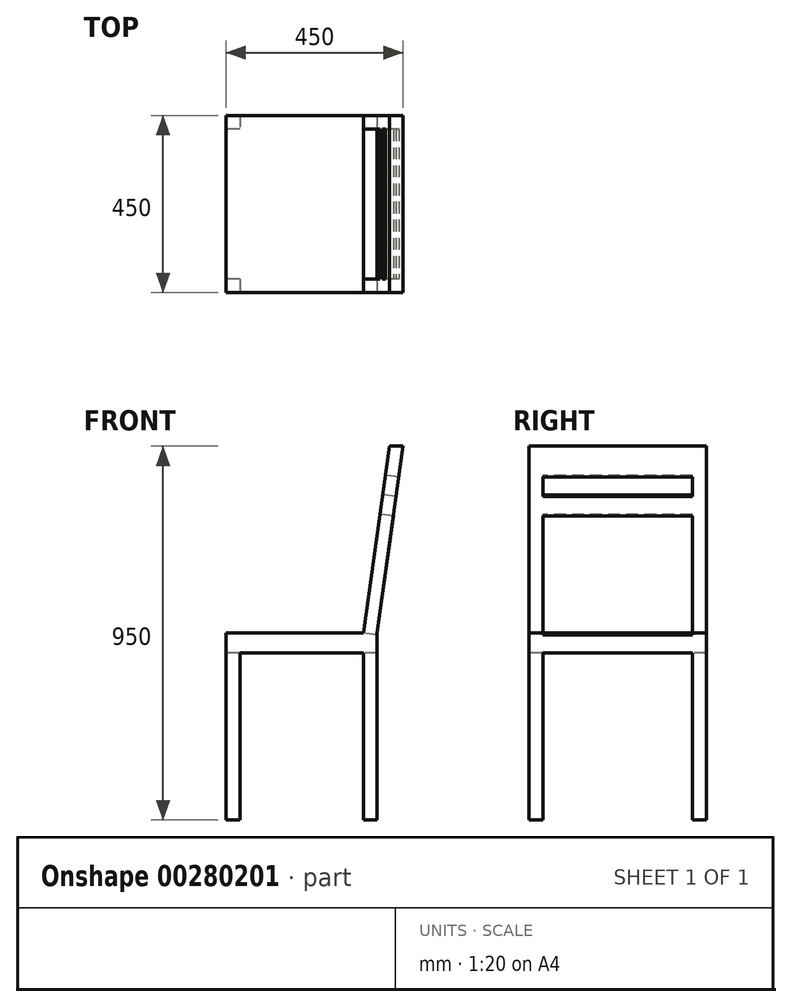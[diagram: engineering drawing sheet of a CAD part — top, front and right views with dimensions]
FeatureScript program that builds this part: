
annotation { "Feature Type Name" : "Feature", "Feature Type Description" : "" }
export const myFeature = defineFeature(function(context is Context, id is Id, definition is map)
    precondition{}
    {
        {
            var Q0;
            Q0=qCreatedBy(makeId("Top.planeOp"),FACE);
            var sketch = newSketch(context, id + "F0", { "sketchPlane" : qUnion([Q0])});
            skLineSegment(sketch, "E0.bottom", {"start": v(225, 225) * mm, "end": v(-225, 225) * mm});
            skLineSegment(sketch, "E0.top", {"start": v(225, -225) * mm, "end": v(-225, -225) * mm});
            skLineSegment(sketch, "E0.left", {"start": v(225, 225) * mm, "end": v(225, -225) * mm});
            skLineSegment(sketch, "E0.right", {"start": v(-225, 225) * mm, "end": v(-225, -225) * mm});
            skPoint(sketch, "E0.middle", {"position": v(0, 0) * mm});
            skSolve(sketch);
        }
        {
            var Q0;
            Q0=qSketchRegion(id+"F0",true);
            extrude(context, id + "F1", {"entities" : qUnion([Q0]), "depth" : 950 * mm});
        }
        {
            var Q0;
            Q0=makeQuery(id+"F1.opExtrude","SWEPT_FACE",FACE,{"disambiguationData":[OSD([sQuery(id+"F0.wireOp",EDGE,"E0.top")])]});
            var sketch = newSketch(context, id + "F2", { "sketchPlane" : qUnion([Q0])});
            skLineSegment(sketch, "E1.bottom", {"start": v(225, 475) * mm, "end": v(-225, 475) * mm});
            skLineSegment(sketch, "E1.top", {"start": v(225, 425) * mm, "end": v(-225, 425) * mm});
            skLineSegment(sketch, "E1.left", {"start": v(225, 475) * mm, "end": v(225, 425) * mm});
            skLineSegment(sketch, "E1.right", {"start": v(-225, 475) * mm, "end": v(-225, 425) * mm});
            skLineSegment(sketch, "E2", {"start": v(225, 950) * mm, "end": v(158.8, 475) * mm});
            skLineSegment(sketch, "E3", {"start": v(190, 950) * mm, "end": v(123.8, 475) * mm});
            skLineSegment(sketch, "E4", {"start": v(158.8, 475) * mm, "end": v(158.8, 0) * mm});
            skLineSegment(sketch, "E5", {"start": v(123.8, 475) * mm, "end": v(123.8, 0) * mm});
            skLineSegment(sketch, "E6.bottom", {"start": v(-225, 0) * mm, "end": v(-190, 0) * mm});
            skLineSegment(sketch, "E6.top", {"start": v(-225, 425) * mm, "end": v(-190, 425) * mm});
            skLineSegment(sketch, "E6.left", {"start": v(-225, 0) * mm, "end": v(-225, 425) * mm});
            skLineSegment(sketch, "E6.right", {"start": v(-190, 0) * mm, "end": v(-190, 425) * mm});
            skSolve(sketch);
        }
        {
            var Q0;
            {var subQ4=sQuery(id+"F2.wireOp",EDGE,"E3");Q0=makeQuery(id+"F2.imprint","IMPRINT",FACE,{"disambiguationData":[TD([[makeQuery(id+"F2.imprint","IMPRINT",EDGE,{"derivedFrom":subQ4}),-1.0]])]});}
            var Q1;
            {var subQ4=sQuery(id+"F2.wireOp",EDGE,"E2");Q1=makeQuery(id+"F2.imprint","IMPRINT",FACE,{"disambiguationData":[TD([[makeQuery(id+"F2.imprint","IMPRINT",EDGE,{"derivedFrom":subQ4}),1.0]])]});}
            var Q2;
            {var subQ1=sQuery(id+"F0.wireOp",EDGE,"E0.top");var subQ4=sQuery(id+"F2.wireOp",EDGE,"E4");var subQ6=makeQuery(id+"F1.opExtrude","CAP_EDGE",EDGE,{"disambiguationData":[OSD([subQ1])],"isStart":true});var subQ7=makeQuery(id+"F2.imprint","INTERSECT",VERTEX,{"derivedFrom":[subQ6,subQ4]});Q2=makeQuery(id+"F2.imprint","IMPRINT",FACE,{"disambiguationData":[TD([[makeQuery(id+"F2.imprint","IMPRINT",EDGE,{"disambiguationData":[TD([[subQ7,1.0]])],"derivedFrom":subQ4}),1.0]])]});}
            var Q3;
            {var subQ0=sQuery(id+"F2.wireOp",EDGE,"E6.right");Q3=makeQuery(id+"F2.imprint","IMPRINT",FACE,{"disambiguationData":[TD([[makeQuery(id+"F2.imprint","IMPRINT",EDGE,{"derivedFrom":subQ0}),-1.0]])]});}
            var Q4;
            {var subQ0=sQuery(id+"F2.wireOp",EDGE,"E1.left");Q4=makeQuery(id+"F2.imprint","IMPRINT",FACE,{"disambiguationData":[TD([[makeQuery(id+"F2.imprint","IMPRINT",EDGE,{"derivedFrom":subQ0}),-1.0]])]});}
            extrude(context, id + "F3", {"entities" : qUnion([Q0, Q1, Q2, Q3, Q4]), "operationType" : NewBodyOperationType.REMOVE, "endBound" : BoundingType.THROUGH_ALL, "oppositeDirection" : true, "depth" : 25 * mm});
        }
        {
            var Q0;
            Q0=makeQuery(id+"F1.opExtrude","SWEPT_FACE",FACE,{"disambiguationData":[OSD([sQuery(id+"F0.wireOp",EDGE,"E0.right")])]});
            var sketch = newSketch(context, id + "F4", { "sketchPlane" : qUnion([Q0])});
            skLineSegment(sketch, "E7", {"start": v(-190, 0) * mm, "end": v(-190, 425) * mm});
            skLineSegment(sketch, "E8", {"start": v(-190, 425) * mm, "end": v(190, 425) * mm});
            skLineSegment(sketch, "E9", {"start": v(190, 425) * mm, "end": v(190, 0) * mm});
            skSolve(sketch);
        }
        {
            var Q0;
            {var subQ0=sQuery(id+"F4.wireOp",EDGE,"E7");Q0=makeQuery(id+"F4.imprint","IMPRINT",FACE,{"disambiguationData":[TD([[makeQuery(id+"F4.imprint","IMPRINT",EDGE,{"derivedFrom":subQ0}),-1.0]])]});}
            extrude(context, id + "F5", {"entities" : qUnion([Q0]), "operationType" : NewBodyOperationType.REMOVE, "endBound" : BoundingType.THROUGH_ALL, "oppositeDirection" : true, "depth" : 25 * mm});
        }
        {
            var Q0;
            Q0=makeQuery(id+"F3.boolean.opBoolean","COPY",FACE,{"derivedFrom":makeQuery(id+"F3.opExtrude","SWEPT_FACE",FACE,{"disambiguationData":[OSD([sQuery(id+"F2.wireOp",EDGE,"E3")])]})});
            var sketch = newSketch(context, id + "F6", { "sketchPlane" : qUnion([Q0])});
            skLineSegment(sketch, "E10", {"start": v(-190, 487.54) * mm, "end": v(-190, 892.13) * mm});
            skLineSegment(sketch, "E11", {"start": v(-190, 892.13) * mm, "end": v(190, 892.13) * mm});
            skLineSegment(sketch, "E12", {"start": v(190, 892.13) * mm, "end": v(190, 487.54) * mm});
            skLineSegment(sketch, "E13", {"start": v(-190, 842.13) * mm, "end": v(190, 842.13) * mm});
            skLineSegment(sketch, "E14", {"start": v(-190, 792.13) * mm, "end": v(190, 792.13) * mm});
            skSolve(sketch);
        }
        {
            var Q0;
            {var subQ0=sQuery(id+"F6.wireOp",EDGE,"E11");Q0=makeQuery(id+"F6.imprint","IMPRINT",FACE,{"disambiguationData":[TD([[makeQuery(id+"F6.imprint","IMPRINT",EDGE,{"derivedFrom":subQ0}),-1.0]])]});}
            var Q1;
            {var subQ3=sQuery(id+"F6.wireOp",EDGE,"E14");Q1=makeQuery(id+"F6.imprint","IMPRINT",FACE,{"disambiguationData":[TD([[makeQuery(id+"F6.imprint","IMPRINT",EDGE,{"derivedFrom":subQ3}),-1.0]])]});}
            extrude(context, id + "F7", {"entities" : qUnion([Q0, Q1]), "operationType" : NewBodyOperationType.REMOVE, "endBound" : BoundingType.THROUGH_ALL, "oppositeDirection" : true, "depth" : 25 * mm});
        }
    });
